# Revit family: Plumbing-Water-Closet-Combos-Sloan-Valve-WETS-20021002_
name_source: partatom
category: Plumbing Fixtures
units: mm (PartAtom-declared; Revit-internal decimal feet)

## family parameters
Cut with Voids When Loaded = No
Host = Face
OmniClass Number = 23.45.05.21.11.11
OmniClass Title = Water Operated Water Closets
Part Type = Normal
Room Calculation Point = No
Round Connector Dimension = Use Diameter
Shared = No

## types (2) — shared parameters
Assembly Code = D2010
CW Connection = Yes
Default Elevation = 0"
Depth = 26 3/4"
Edition number = 1
Flush Rate = 1.6/1.1 gpf (6.0/4.2 Lpf)
Flushometer Code = 3720000
Flushometer Material = Sloan Valve - Finish - Polished Chrome
HW Connection = Yes
Height = 15"
Keynote = 15410
Manufacturer = Sloan Valve
Product Material = Sloan Valve - Vitreous China - White
Product data url = https://bimobject.com
Sanitary Drain Connection Diameter = 2"
URL = www.sloanvalve.com
Valve Pressure Drop = 0.00 psi
Vent Connection = Yes
WFU = 10
Waste Connection = Yes
Water Closet Code = 2102009
Water Inlet Connection Diameter = 1"
Width = 14"
zero-valued in all types: CWFU, HWFU

## per-type parameters (varying)
| type | Description | Part Number |
| WETS-2002.1002 | ST-2009 Water Closet and WES 111 Flushometer. | 20021002 |
| WETS-2002.1002-CO | Carbon Offset, ST-2009 Water Closet and WES 111 Flushometer. | 20021002T |

note: column(s) folded — value = type name in every type: Model

## geometry (parser evidence)
native form markers: Sweep x3
no freeform markers — native parametric forms only
